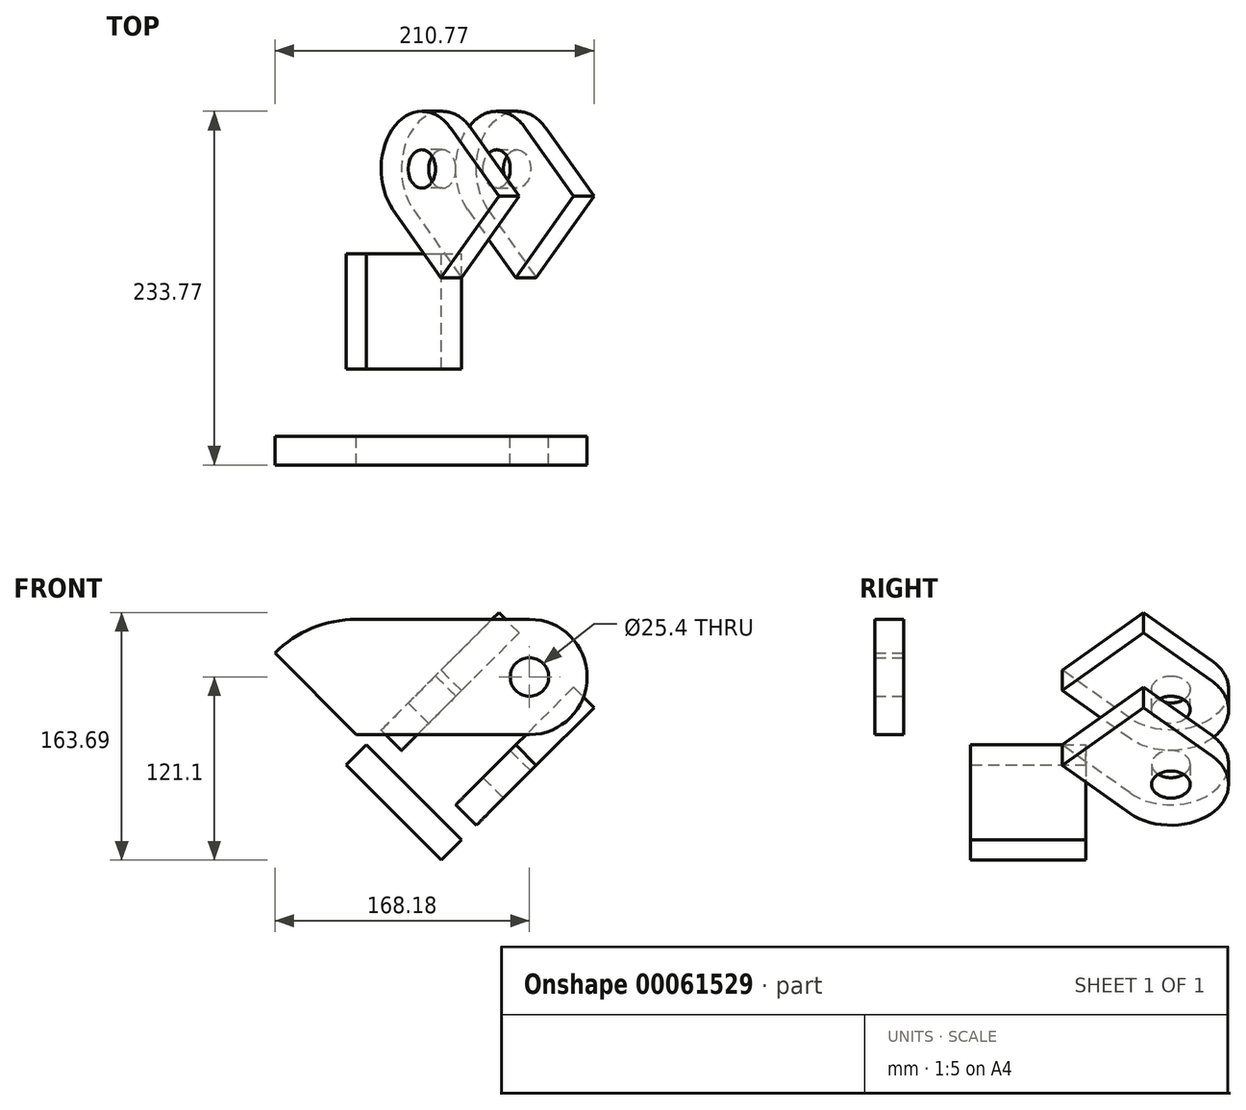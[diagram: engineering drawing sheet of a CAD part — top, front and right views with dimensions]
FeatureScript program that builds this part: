
annotation { "Feature Type Name" : "Feature", "Feature Type Description" : "" }
export const myFeature = defineFeature(function(context is Context, id is Id, definition is map)
    precondition{}
    {
        {
            var Q0;
            Q0=qCreatedBy(makeId("Front.planeOp"),FACE);
            var sketch = newSketch(context, id + "F0", { "sketchPlane" : qUnion([Q0])});
            skCircle(sketch, "E0", {"center": v(0, 0) * mm, "radius": 12.7 * mm});
            skLineSegment(sketch, "E1", {"start": v(0, 0) * mm, "end": v(0, -38.1) * mm, "construction": true});
            skLineSegment(sketch, "E2", {"start": v(0, -38.1) * mm, "end": v(-114.3, -38.1) * mm});
            skLineSegment(sketch, "E3", {"start": v(0, 0) * mm, "end": v(0, 38.1) * mm, "construction": true});
            skArc(sketch, "E4", {"start": v(0, -38.1) * mm, "mid": v(38.1, 0) * mm, "end": v(0, 38.1) * mm});
            skLineSegment(sketch, "E5", {"start": v(-114.3, -38.1) * mm, "end": v(-168.18, 15.78) * mm});
            skLineSegment(sketch, "E6", {"start": v(0, 38.1) * mm, "end": v(-114.3, 38.1) * mm});
            skArc(sketch, "E7", {"start": v(-114.3, 38.1) * mm, "mid": v(-143.46, 32.3) * mm, "end": v(-168.18, 15.78) * mm});
            skSolve(sketch);
        }
        {
            var Q0;
            Q0 = qSketchRegion(id + "F0", true);
            extrude(context, id + "F1", {"entities" : qUnion([Q0]), "endBound" : BoundingType.SYMMETRIC, "depth" : 19.05 * mm});
        }
        {
            var Q0;
            Q0=makeQuery(id+"F1.opExtrude","SWEPT_FACE",FACE,{"disambiguationData":[OSD([sQuery(id+"F0.wireOp",EDGE,"E5")])]});
            var sketch = newSketch(context, id + "F2", { "sketchPlane" : qUnion([Q0])});
            skLineSegment(sketch, "E8.rect.bottom", {"start": v(-53.88, 44.45) * mm, "end": v(-130.08, 44.45) * mm});
            skLineSegment(sketch, "E8.rect.top", {"start": v(-53.88, -44.45) * mm, "end": v(-130.08, -44.45) * mm});
            skLineSegment(sketch, "E8.rect.left", {"start": v(-53.88, 44.45) * mm, "end": v(-53.88, -44.45) * mm});
            skLineSegment(sketch, "E8.rect.right", {"start": v(-130.08, 44.45) * mm, "end": v(-130.08, -44.45) * mm});
            skPoint(sketch, "E8.rect.middle", {"position": v(-91.98, 0) * mm});
            skSolve(sketch);
        }
        {
            var Q0;
            Q0 = qSketchRegion(id + "F2", true);
            extrude(context, id + "F3", {"entities" : qUnion([Q0]), "operationType" : NewBodyOperationType.ADD, "depth" : 19.05 * mm});
        }
        {
            var Q0;
            Q0=makeQuery(id+"F3.opExtrude","SWEPT_FACE",FACE,{"disambiguationData":[OSD([sQuery(id+"F2.wireOp",EDGE,"E8.rect.bottom")])]});
            var sketch = newSketch(context, id + "F4", { "sketchPlane" : qUnion([Q0])});
            skLineSegment(sketch, "E9", {"start": v(-154.71, -24.63) * mm, "end": v(-186.14, -56.06) * mm, "construction": true});
            skCircle(sketch, "E10", {"center": v(-186.14, -56.06) * mm, "radius": 12.7 * mm});
            skLineSegment(sketch, "E11", {"start": v(-159.2, -83) * mm, "end": v(-114.3, -38.1) * mm});
            skLineSegment(sketch, "E12", {"start": v(-168.18, 15.78) * mm, "end": v(-213.08, -29.12) * mm});
            skLineSegment(sketch, "E13", {"start": v(-213.08, -29.12) * mm, "end": v(-186.14, -56.06) * mm, "construction": true});
            skLineSegment(sketch, "E14", {"start": v(-186.14, -56.06) * mm, "end": v(-159.2, -83) * mm, "construction": true});
            skArc(sketch, "E15", {"start": v(-213.08, -29.12) * mm, "mid": v(-213.08, -83) * mm, "end": v(-159.2, -83) * mm});
            skLineSegment(sketch, "E16", {"start": v(-168.18, 15.78) * mm, "end": v(-114.3, -38.1) * mm});
            skSolve(sketch);
        }
        {
            var Q0;
            Q0 = qSketchRegion(id + "F4", true);
            extrude(context, id + "F5", {"entities" : qUnion([Q0]), "operationType" : NewBodyOperationType.ADD, "oppositeDirection" : true, "depth" : 19.05 * mm});
        }
        {
            var Q0;
            Q0=makeQuery(id+"F3.opExtrude","SWEPT_FACE",FACE,{"disambiguationData":[OSD([sQuery(id+"F2.wireOp",EDGE,"E8.rect.top")])]});
            var sketch = newSketch(context, id + "F6", { "sketchPlane" : qUnion([Q0])});
            skLineSegment(sketch, "E17.0", {"start": v(168.18, 15.78) * mm, "end": v(114.3, -38.1) * mm});
            skLineSegment(sketch, "E18.0", {"start": v(168.18, 15.78) * mm, "end": v(213.08, -29.12) * mm});
            skArc(sketch, "E19.0", {"start": v(213.08, -29.12) * mm, "mid": v(213.08, -83) * mm, "end": v(159.2, -83) * mm});
            skLineSegment(sketch, "E20.0", {"start": v(159.2, -83) * mm, "end": v(114.3, -38.1) * mm});
            skCircle(sketch, "E21.0", {"center": v(186.14, -56.06) * mm, "radius": 12.7 * mm});
            skSolve(sketch);
        }
        {
            var Q0;
            Q0 = qSketchRegion(id + "F6", true);
            extrude(context, id + "F7", {"entities" : qUnion([Q0]), "operationType" : NewBodyOperationType.ADD, "oppositeDirection" : true, "depth" : 19.05 * mm});
        }
    });
